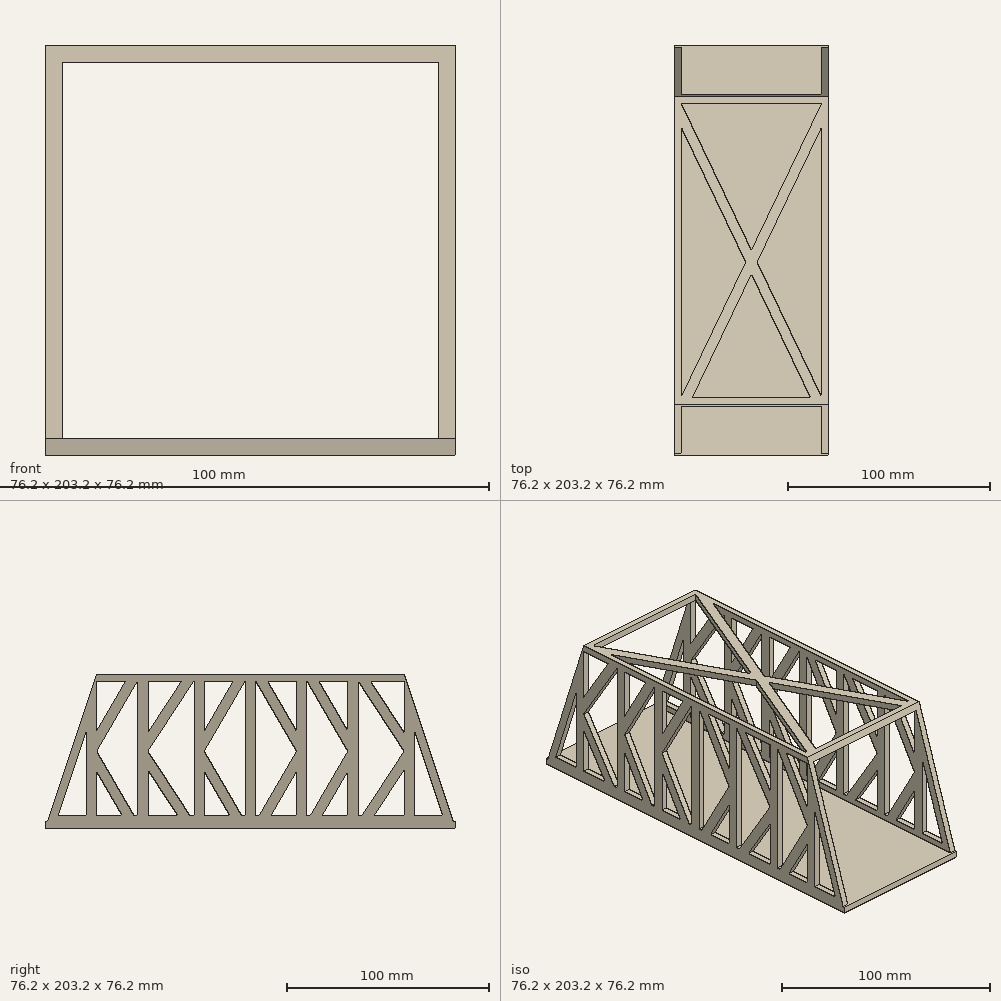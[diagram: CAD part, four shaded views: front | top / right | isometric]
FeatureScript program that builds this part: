
annotation { "Feature Type Name" : "Feature", "Feature Type Description" : "" }
export const myFeature = defineFeature(function(context is Context, id is Id, definition is map)
    precondition{}
    {
        {
            var Q0;
            Q0=qCreatedBy(makeId("Right.planeOp"),FACE);
            var sketch = newSketch(context, id + "F0", { "sketchPlane" : qUnion([Q0])});
            skLineSegment(sketch, "E0", {"start": v(-101.6, -38.1) * mm, "end": v(101.6, -38.1) * mm});
            skLineSegment(sketch, "E1", {"start": v(-76.2, 38.1) * mm, "end": v(76.2, 38.1) * mm});
            skLineSegment(sketch, "E2", {"start": v(-76.2, 38.1) * mm, "end": v(-101.6, -38.1) * mm});
            skLineSegment(sketch, "E3", {"start": v(76.2, 38.1) * mm, "end": v(101.6, -38.1) * mm});
            skSolve(sketch);
        }
        {
            var Q0;
            Q0=qSketchRegion(id+"F0",true);
            extrude(context, id + "F1", {"entities" : qUnion([Q0]), "endBound" : BoundingType.SYMMETRIC, "depth" : 76.2 * mm, "offsetDistance" : 25.4 * mm});
        }
        {
            var Q0;
            Q0=qCreatedBy(makeId("Front.planeOp"),FACE);
            var sketch = newSketch(context, id + "F2", { "sketchPlane" : qUnion([Q0])});
            skLineSegment(sketch, "E4.bottom", {"start": v(34.92, -34.92) * mm, "end": v(-34.92, -34.93) * mm});
            skLineSegment(sketch, "E4.top", {"start": v(34.92, 34.93) * mm, "end": v(-34.92, 34.92) * mm});
            skLineSegment(sketch, "E4.left", {"start": v(-34.92, -34.92) * mm, "end": v(-34.92, 34.92) * mm});
            skLineSegment(sketch, "E4.right", {"start": v(34.92, -34.92) * mm, "end": v(34.92, 34.92) * mm});
            skPoint(sketch, "E4.middle", {"position": v(0, 0) * mm});
            skSolve(sketch);
        }
        {
            var Q0;
            Q0=qSketchRegion(id+"F2",true);
            extrude(context, id + "F3", {"entities" : qUnion([Q0]), "operationType" : NewBodyOperationType.REMOVE, "endBound" : BoundingType.SYMMETRIC, "oppositeDirection" : true, "depth" : 254 * mm, "offsetDistance" : 25.4 * mm});
        }
        {
            var Q0;
            Q0=makeQuery(id+"F1.opExtrude","CAP_FACE",FACE,{"disambiguationData":[OSD([sQuery(id+"F0.wireOp",EDGE,"E0"),sQuery(id+"F0.wireOp",EDGE,"E1"),sQuery(id+"F0.wireOp",EDGE,"E2"),sQuery(id+"F0.wireOp",EDGE,"E3")])],"isStart":false});
            var sketch = newSketch(context, id + "F4", { "sketchPlane" : qUnion([Q0])});
            skLineSegment(sketch, "E5.bottom", {"start": v(76.2, -34.92) * mm, "end": v(-76.2, -34.92) * mm});
            skLineSegment(sketch, "E5.top", {"start": v(76.2, 34.92) * mm, "end": v(-76.2, 34.92) * mm});
            skLineSegment(sketch, "E5.left", {"start": v(76.2, -34.92) * mm, "end": v(76.2, 34.92) * mm});
            skLineSegment(sketch, "E5.right", {"start": v(-76.2, -34.92) * mm, "end": v(-76.2, 34.92) * mm});
            skPoint(sketch, "E5.middle", {"position": v(0, 0) * mm});
            skLineSegment(sketch, "E6.bottom", {"start": v(2.54, -34.92) * mm, "end": v(-2.54, -34.92) * mm});
            skLineSegment(sketch, "E6.top", {"start": v(2.54, 34.92) * mm, "end": v(-2.54, 34.92) * mm});
            skLineSegment(sketch, "E6.left", {"start": v(2.54, -34.93) * mm, "end": v(2.54, 34.93) * mm});
            skLineSegment(sketch, "E6.right", {"start": v(-2.54, -34.93) * mm, "end": v(-2.54, 34.93) * mm});
            skLineSegment(sketch, "E7.bottom", {"start": v(-50.8, -34.92) * mm, "end": v(-55.88, -34.92) * mm});
            skLineSegment(sketch, "E7.top", {"start": v(-50.8, 34.92) * mm, "end": v(-55.88, 34.92) * mm});
            skLineSegment(sketch, "E7.left", {"start": v(-50.8, -34.93) * mm, "end": v(-50.8, 34.93) * mm});
            skLineSegment(sketch, "E7.right", {"start": v(-55.88, -34.93) * mm, "end": v(-55.88, 34.93) * mm});
            skPoint(sketch, "E7.middle", {"position": v(-53.34, 0) * mm});
            skLineSegment(sketch, "E8.bottom", {"start": v(-22.86, -34.92) * mm, "end": v(-27.94, -34.92) * mm});
            skLineSegment(sketch, "E8.top", {"start": v(-22.86, 34.92) * mm, "end": v(-27.94, 34.92) * mm});
            skLineSegment(sketch, "E8.left", {"start": v(-22.86, -34.92) * mm, "end": v(-22.86, 34.92) * mm});
            skLineSegment(sketch, "E8.right", {"start": v(-27.94, -34.92) * mm, "end": v(-27.94, 34.92) * mm});
            skPoint(sketch, "E8.middle", {"position": v(-25.4, 0) * mm});
            skLineSegment(sketch, "E9.bottom", {"start": v(27.94, -34.92) * mm, "end": v(22.86, -34.92) * mm});
            skLineSegment(sketch, "E9.top", {"start": v(27.94, 34.92) * mm, "end": v(22.86, 34.92) * mm});
            skLineSegment(sketch, "E9.left", {"start": v(27.94, -34.92) * mm, "end": v(27.94, 34.92) * mm});
            skLineSegment(sketch, "E9.right", {"start": v(22.86, -34.93) * mm, "end": v(22.86, 34.92) * mm});
            skPoint(sketch, "E9.middle", {"position": v(25.4, 0) * mm});
            skLineSegment(sketch, "E10.bottom", {"start": v(53.34, -34.92) * mm, "end": v(48.26, -34.92) * mm});
            skLineSegment(sketch, "E10.top", {"start": v(53.34, 34.92) * mm, "end": v(48.26, 34.92) * mm});
            skLineSegment(sketch, "E10.left", {"start": v(53.34, -34.93) * mm, "end": v(53.34, 34.93) * mm});
            skLineSegment(sketch, "E10.right", {"start": v(48.26, -34.93) * mm, "end": v(48.26, 34.93) * mm});
            skPoint(sketch, "E10.middle", {"position": v(50.8, 0) * mm});
            skLineSegment(sketch, "E11", {"start": v(-55.88, 34.92) * mm, "end": v(-76.2, 0) * mm});
            skLineSegment(sketch, "E12", {"start": v(-76.2, 0) * mm, "end": v(-55.88, -34.92) * mm});
            skLineSegment(sketch, "E13", {"start": v(-27.94, 34.92) * mm, "end": v(-50.8, 0) * mm});
            skLineSegment(sketch, "E14", {"start": v(-50.8, 0) * mm, "end": v(-27.94, -34.92) * mm});
            skLineSegment(sketch, "E15", {"start": v(-2.54, 34.92) * mm, "end": v(-22.86, 0) * mm});
            skLineSegment(sketch, "E16", {"start": v(-22.86, 0) * mm, "end": v(-2.54, -34.92) * mm});
            skLineSegment(sketch, "E17", {"start": v(2.54, 34.92) * mm, "end": v(22.86, 0) * mm});
            skLineSegment(sketch, "E18", {"start": v(22.86, 0) * mm, "end": v(2.54, -34.92) * mm});
            skLineSegment(sketch, "E19", {"start": v(27.94, 34.93) * mm, "end": v(48.26, 0) * mm});
            skLineSegment(sketch, "E20", {"start": v(48.26, 0) * mm, "end": v(27.94, -34.93) * mm});
            skLineSegment(sketch, "E21", {"start": v(53.34, 34.92) * mm, "end": v(76.2, 0) * mm});
            skLineSegment(sketch, "E22", {"start": v(76.2, 0) * mm, "end": v(53.34, -34.92) * mm});
            skLineSegment(sketch, "E23", {"start": v(-76.2, -10.1) * mm, "end": v(-61.76, -34.93) * mm});
            skLineSegment(sketch, "E24", {"start": v(-34.01, 34.93) * mm, "end": v(-50.8, 9.28) * mm});
            skLineSegment(sketch, "E25", {"start": v(-50.8, -9.28) * mm, "end": v(-34.01, -34.93) * mm});
            skLineSegment(sketch, "E26", {"start": v(-8.42, 34.93) * mm, "end": v(-22.86, 10.1) * mm});
            skLineSegment(sketch, "E27", {"start": v(-22.86, -10.1) * mm, "end": v(-8.42, -34.93) * mm});
            skLineSegment(sketch, "E28", {"start": v(-61.76, 34.93) * mm, "end": v(-76.2, 10.1) * mm});
            skLineSegment(sketch, "E29", {"start": v(8.42, 34.93) * mm, "end": v(22.86, 10.1) * mm});
            skLineSegment(sketch, "E30", {"start": v(22.86, -10.1) * mm, "end": v(8.42, -34.93) * mm});
            skLineSegment(sketch, "E31", {"start": v(33.82, 34.93) * mm, "end": v(48.26, 10.1) * mm});
            skLineSegment(sketch, "E32", {"start": v(48.26, -10.1) * mm, "end": v(33.82, -34.93) * mm});
            skLineSegment(sketch, "E33", {"start": v(59.41, 34.93) * mm, "end": v(76.2, 9.28) * mm});
            skLineSegment(sketch, "E34", {"start": v(76.2, -9.28) * mm, "end": v(59.41, -34.93) * mm});
            skLineSegment(sketch, "E35", {"start": v(-81.28, -34.93) * mm, "end": v(-81.28, 10.1) * mm});
            skLineSegment(sketch, "E36", {"start": v(-81.28, 10.1) * mm, "end": v(-96.29, -34.93) * mm});
            skLineSegment(sketch, "E37", {"start": v(-96.29, -34.92) * mm, "end": v(-81.28, -34.92) * mm});
            skLineSegment(sketch, "E38.MirrorCS", {"start": v(81.28, -34.93) * mm, "end": v(81.28, 10.1) * mm});
            skLineSegment(sketch, "E39.MirrorCS", {"start": v(81.28, 10.1) * mm, "end": v(96.29, -34.93) * mm});
            skLineSegment(sketch, "E40.MirrorCS", {"start": v(96.29, -34.92) * mm, "end": v(81.28, -34.92) * mm});
            skSolve(sketch);
        }
        {
            var Q0;
            Q0=makeQuery(id+"F4.imprint","IMPRINT",FACE,{"disambiguationData":[TD([[makeQuery(id+"F4.imprint","IMPRINT",EDGE,{"derivedFrom":sQuery(id+"F4.wireOp",EDGE,"E35")}),1.0]])]});
            var Q1;
            {var subQ3=sQuery(id+"F4.wireOp",EDGE,"E28");Q1=makeQuery(id+"F4.imprint","IMPRINT",FACE,{"disambiguationData":[TD([[makeQuery(id+"F4.imprint","IMPRINT",EDGE,{"derivedFrom":subQ3}),-1.0]])]});}
            var Q2;
            Q2=makeQuery(id+"F4.imprint","IMPRINT",FACE,{"disambiguationData":[TD([[makeQuery(id+"F4.imprint","IMPRINT",EDGE,{"derivedFrom":sQuery(id+"F4.wireOp",EDGE,"E7.right")}),1.0]])]});
            var Q3;
            {var subQ3=sQuery(id+"F4.wireOp",EDGE,"E23");Q3=makeQuery(id+"F4.imprint","IMPRINT",FACE,{"disambiguationData":[TD([[makeQuery(id+"F4.imprint","IMPRINT",EDGE,{"derivedFrom":subQ3}),-1.0]])]});}
            var Q4;
            {var subQ3=sQuery(id+"F4.wireOp",EDGE,"E24");Q4=makeQuery(id+"F4.imprint","IMPRINT",FACE,{"disambiguationData":[TD([[makeQuery(id+"F4.imprint","IMPRINT",EDGE,{"derivedFrom":subQ3}),-1.0]])]});}
            var Q5;
            Q5=makeQuery(id+"F4.imprint","IMPRINT",FACE,{"disambiguationData":[TD([[makeQuery(id+"F4.imprint","IMPRINT",EDGE,{"derivedFrom":sQuery(id+"F4.wireOp",EDGE,"E8.right")}),1.0]])]});
            var Q6;
            {var subQ3=sQuery(id+"F4.wireOp",EDGE,"E25");Q6=makeQuery(id+"F4.imprint","IMPRINT",FACE,{"disambiguationData":[TD([[makeQuery(id+"F4.imprint","IMPRINT",EDGE,{"derivedFrom":subQ3}),-1.0]])]});}
            var Q7;
            {var subQ3=sQuery(id+"F4.wireOp",EDGE,"E26");Q7=makeQuery(id+"F4.imprint","IMPRINT",FACE,{"disambiguationData":[TD([[makeQuery(id+"F4.imprint","IMPRINT",EDGE,{"derivedFrom":subQ3}),-1.0]])]});}
            var Q8;
            Q8=makeQuery(id+"F4.imprint","IMPRINT",FACE,{"disambiguationData":[TD([[makeQuery(id+"F4.imprint","IMPRINT",EDGE,{"derivedFrom":sQuery(id+"F4.wireOp",EDGE,"E6.right")}),1.0]])]});
            var Q9;
            {var subQ3=sQuery(id+"F4.wireOp",EDGE,"E27");Q9=makeQuery(id+"F4.imprint","IMPRINT",FACE,{"disambiguationData":[TD([[makeQuery(id+"F4.imprint","IMPRINT",EDGE,{"derivedFrom":subQ3}),-1.0]])]});}
            var Q10;
            Q10=makeQuery(id+"F4.imprint","IMPRINT",FACE,{"disambiguationData":[TD([[makeQuery(id+"F4.imprint","IMPRINT",EDGE,{"derivedFrom":sQuery(id+"F4.wireOp",EDGE,"E6.left")}),-1.0]])]});
            var Q11;
            {var subQ3=sQuery(id+"F4.wireOp",EDGE,"E29");Q11=makeQuery(id+"F4.imprint","IMPRINT",FACE,{"disambiguationData":[TD([[makeQuery(id+"F4.imprint","IMPRINT",EDGE,{"derivedFrom":subQ3}),1.0]])]});}
            var Q12;
            Q12=makeQuery(id+"F4.imprint","IMPRINT",FACE,{"disambiguationData":[TD([[makeQuery(id+"F4.imprint","IMPRINT",EDGE,{"derivedFrom":sQuery(id+"F4.wireOp",EDGE,"E9.left")}),-1.0]])]});
            var Q13;
            {var subQ3=sQuery(id+"F4.wireOp",EDGE,"E30");Q13=makeQuery(id+"F4.imprint","IMPRINT",FACE,{"disambiguationData":[TD([[makeQuery(id+"F4.imprint","IMPRINT",EDGE,{"derivedFrom":subQ3}),1.0]])]});}
            var Q14;
            {var subQ3=sQuery(id+"F4.wireOp",EDGE,"E31");Q14=makeQuery(id+"F4.imprint","IMPRINT",FACE,{"disambiguationData":[TD([[makeQuery(id+"F4.imprint","IMPRINT",EDGE,{"derivedFrom":subQ3}),1.0]])]});}
            var Q15;
            {var subQ3=sQuery(id+"F4.wireOp",EDGE,"E32");Q15=makeQuery(id+"F4.imprint","IMPRINT",FACE,{"disambiguationData":[TD([[makeQuery(id+"F4.imprint","IMPRINT",EDGE,{"derivedFrom":subQ3}),1.0]])]});}
            var Q16;
            Q16=makeQuery(id+"F4.imprint","IMPRINT",FACE,{"disambiguationData":[TD([[makeQuery(id+"F4.imprint","IMPRINT",EDGE,{"derivedFrom":sQuery(id+"F4.wireOp",EDGE,"E10.left")}),-1.0]])]});
            var Q17;
            {var subQ3=sQuery(id+"F4.wireOp",EDGE,"E33");Q17=makeQuery(id+"F4.imprint","IMPRINT",FACE,{"disambiguationData":[TD([[makeQuery(id+"F4.imprint","IMPRINT",EDGE,{"derivedFrom":subQ3}),1.0]])]});}
            var Q18;
            {var subQ3=sQuery(id+"F4.wireOp",EDGE,"E34");Q18=makeQuery(id+"F4.imprint","IMPRINT",FACE,{"disambiguationData":[TD([[makeQuery(id+"F4.imprint","IMPRINT",EDGE,{"derivedFrom":subQ3}),1.0]])]});}
            var Q19;
            Q19=makeQuery(id+"F4.imprint","IMPRINT",FACE,{"disambiguationData":[TD([[makeQuery(id+"F4.imprint","IMPRINT",EDGE,{"derivedFrom":sQuery(id+"F4.wireOp",EDGE,"E38.MirrorCS")}),-1.0]])]});
            extrude(context, id + "F5", {"entities" : qUnion([Q0, Q1, Q2, Q3, Q4, Q5, Q6, Q7, Q8, Q9, Q10, Q11, Q12, Q13, Q14, Q15, Q16, Q17, Q18, Q19]), "operationType" : NewBodyOperationType.REMOVE, "oppositeDirection" : true, "depth" : 76.2 * mm, "offsetDistance" : 25.4 * mm});
        }
        {
            var Q0;
            Q0=makeQuery(id+"F1.opExtrude","CAP_FACE",FACE,{"disambiguationData":[OSD([sQuery(id+"F0.wireOp",EDGE,"E0"),sQuery(id+"F0.wireOp",EDGE,"E1"),sQuery(id+"F0.wireOp",EDGE,"E2"),sQuery(id+"F0.wireOp",EDGE,"E3")])],"isStart":false});
            var sketch = newSketch(context, id + "F6", { "sketchPlane" : qUnion([Q0])});
            skLineSegment(sketch, "E41.bottom", {"start": v(-96.29, -34.93) * mm, "end": v(-101.6, -34.93) * mm});
            skLineSegment(sketch, "E41.top", {"start": v(-96.29, -38.1) * mm, "end": v(-101.6, -38.1) * mm});
            skLineSegment(sketch, "E41.left", {"start": v(-96.29, -34.93) * mm, "end": v(-96.29, -38.1) * mm});
            skLineSegment(sketch, "E41.right", {"start": v(-101.6, -34.93) * mm, "end": v(-101.6, -38.1) * mm});
            skLineSegment(sketch, "E42.MirrorCS", {"start": v(96.29, -34.93) * mm, "end": v(101.6, -34.93) * mm});
            skLineSegment(sketch, "E43.MirrorCS", {"start": v(101.6, -34.93) * mm, "end": v(101.6, -38.1) * mm});
            skLineSegment(sketch, "E44.MirrorCS", {"start": v(96.29, -34.93) * mm, "end": v(96.29, -38.1) * mm});
            skLineSegment(sketch, "E45.MirrorCS", {"start": v(96.29, -38.1) * mm, "end": v(101.6, -38.1) * mm});
            skSolve(sketch);
        }
        {
            var Q0;
            Q0=qSketchRegion(id+"F6",true);
            extrude(context, id + "F7", {"entities" : qUnion([Q0]), "operationType" : NewBodyOperationType.ADD, "oppositeDirection" : true, "depth" : 76.2 * mm, "offsetDistance" : 25.4 * mm});
        }
        {
            var Q0;
            Q0=makeQuery(id+"F1.opExtrude","SWEPT_FACE",FACE,{"disambiguationData":[OSD([sQuery(id+"F0.wireOp",EDGE,"E1")])]});
            var sketch = newSketch(context, id + "F8", { "sketchPlane" : qUnion([Q0])});
            skLineSegment(sketch, "E46.bottom", {"start": v(34.92, -73.03) * mm, "end": v(-34.93, -73.03) * mm});
            skLineSegment(sketch, "E46.top", {"start": v(34.92, 73.03) * mm, "end": v(-34.93, 73.03) * mm});
            skLineSegment(sketch, "E46.left", {"start": v(34.92, -73.03) * mm, "end": v(34.92, 73.03) * mm});
            skLineSegment(sketch, "E46.right", {"start": v(-34.92, -73.03) * mm, "end": v(-34.92, 73.03) * mm});
            skPoint(sketch, "E46.middle", {"position": v(0, 0) * mm});
            skLineSegment(sketch, "E47", {"start": v(-34.92, 73.03) * mm, "end": v(34.92, -73.03) * mm});
            skLineSegment(sketch, "E48", {"start": v(-34.92, -73.03) * mm, "end": v(34.92, 73.03) * mm});
            skLineSegment(sketch, "E49", {"start": v(-34.92, 61.25) * mm, "end": v(29.3, -73.03) * mm});
            skLineSegment(sketch, "E50", {"start": v(34.92, 61.25) * mm, "end": v(-29.3, -73.03) * mm});
            skSolve(sketch);
        }
        {
            var Q0;
            {var subQ1=sQuery(id+"F8.wireOp",EDGE,"E46.right");var subQ3=sQuery(id+"F8.wireOp",EDGE,"E49");var subQ4=makeQuery(id+"F8.imprint","INTERSECT",VERTEX,{"derivedFrom":[subQ1,subQ3]});Q0=makeQuery(id+"F8.imprint","IMPRINT",FACE,{"disambiguationData":[TD([[makeQuery(id+"F8.imprint","IMPRINT",EDGE,{"disambiguationData":[TD([[subQ4,-1.0]])],"derivedFrom":subQ3}),-1.0]])]});}
            var Q1;
            {var subQ0=sQuery(id+"F8.wireOp",EDGE,"E46.top");Q1=makeQuery(id+"F8.imprint","IMPRINT",FACE,{"disambiguationData":[TD([[makeQuery(id+"F8.imprint","IMPRINT",EDGE,{"derivedFrom":subQ0}),1.0]])]});}
            var Q2;
            {var subQ1=sQuery(id+"F8.wireOp",EDGE,"E46.left");var subQ3=sQuery(id+"F8.wireOp",EDGE,"E50");var subQ4=makeQuery(id+"F8.imprint","INTERSECT",VERTEX,{"derivedFrom":[subQ1,subQ3]});Q2=makeQuery(id+"F8.imprint","IMPRINT",FACE,{"disambiguationData":[TD([[makeQuery(id+"F8.imprint","IMPRINT",EDGE,{"disambiguationData":[TD([[subQ4,-1.0]])],"derivedFrom":subQ3}),1.0]])]});}
            var Q3;
            {var subQ0=sQuery(id+"F8.wireOp",EDGE,"E49");var subQ1=sQuery(id+"F8.wireOp",EDGE,"E46.bottom");var subQ2=makeQuery(id+"F8.imprint","INTERSECT",VERTEX,{"derivedFrom":[subQ1,subQ0]});Q3=makeQuery(id+"F8.imprint","IMPRINT",FACE,{"disambiguationData":[TD([[makeQuery(id+"F8.imprint","IMPRINT",EDGE,{"disambiguationData":[TD([[subQ2,-1.0]])],"derivedFrom":subQ1}),-1.0]])]});}
            extrude(context, id + "F9", {"entities" : qUnion([Q0, Q1, Q2, Q3]), "operationType" : NewBodyOperationType.REMOVE, "oppositeDirection" : true, "depth" : 3.17 * mm, "offsetDistance" : 25.4 * mm});
        }
        {
            var Q0;
            {var subQ0=sQuery(id+"F4.wireOp",EDGE,"E5.bottom");Q0=makeQuery(id+"F7.boolean.opBoolean","MERGE",FACE,{"derivedFrom":[makeQuery(id+"F5.boolean.opBoolean","MERGE",FACE,{"derivedFrom":[makeQuery(id+"F3.boolean.opBoolean","COPY",FACE,{"derivedFrom":makeQuery(id+"F3.opExtrude","SWEPT_FACE",FACE,{"disambiguationData":[OSD([sQuery(id+"F2.wireOp",EDGE,"E4.bottom")])]})})],"fromTools":[makeQuery(id+"F5.opExtrude","SWEPT_FACE",FACE,{"disambiguationData":[OSD([subQ0]),TDD([makeQuery(id+"F4.imprint","IMPRINT",EDGE,{"disambiguationData":[TD([[makeQuery(id+"F4.imprint","INTERSECT",VERTEX,{"derivedFrom":[subQ0,sQuery(id+"F4.wireOp",EDGE,"E5.left")]}),-1.0]])],"derivedFrom":subQ0})])]}),makeQuery(id+"F5.opExtrude","SWEPT_FACE",FACE,{"disambiguationData":[OSD([subQ0]),TDD([makeQuery(id+"F4.imprint","IMPRINT",EDGE,{"disambiguationData":[TD([[makeQuery(id+"F4.imprint","INTERSECT",VERTEX,{"derivedFrom":[subQ0,sQuery(id+"F4.wireOp",EDGE,"E32")]}),1.0]])],"derivedFrom":subQ0})])]}),makeQuery(id+"F5.opExtrude","SWEPT_FACE",FACE,{"disambiguationData":[OSD([subQ0]),TDD([makeQuery(id+"F4.imprint","IMPRINT",EDGE,{"disambiguationData":[TD([[makeQuery(id+"F4.imprint","INTERSECT",VERTEX,{"derivedFrom":[subQ0,sQuery(id+"F4.wireOp",EDGE,"E30")]}),1.0]])],"derivedFrom":subQ0})])]}),makeQuery(id+"F5.opExtrude","SWEPT_FACE",FACE,{"disambiguationData":[OSD([subQ0]),TDD([makeQuery(id+"F4.imprint","IMPRINT",EDGE,{"disambiguationData":[TD([[makeQuery(id+"F4.imprint","INTERSECT",VERTEX,{"derivedFrom":[subQ0,sQuery(id+"F4.wireOp",EDGE,"E27")]}),-1.0]])],"derivedFrom":subQ0})])]}),makeQuery(id+"F5.opExtrude","SWEPT_FACE",FACE,{"disambiguationData":[OSD([subQ0]),TDD([makeQuery(id+"F4.imprint","IMPRINT",EDGE,{"disambiguationData":[TD([[makeQuery(id+"F4.imprint","INTERSECT",VERTEX,{"derivedFrom":[subQ0,sQuery(id+"F4.wireOp",EDGE,"E25")]}),-1.0]])],"derivedFrom":subQ0})])]}),makeQuery(id+"F5.opExtrude","SWEPT_FACE",FACE,{"disambiguationData":[OSD([subQ0]),TDD([makeQuery(id+"F4.imprint","IMPRINT",EDGE,{"disambiguationData":[TD([[makeQuery(id+"F4.imprint","INTERSECT",VERTEX,{"derivedFrom":[subQ0,sQuery(id+"F4.wireOp",EDGE,"E5.right")]}),1.0]])],"derivedFrom":subQ0})])]}),makeQuery(id+"F5.opExtrude","SWEPT_FACE",FACE,{"disambiguationData":[OSD([sQuery(id+"F4.wireOp",EDGE,"E37")])]}),makeQuery(id+"F5.opExtrude","SWEPT_FACE",FACE,{"disambiguationData":[OSD([sQuery(id+"F4.wireOp",EDGE,"E40.MirrorCS")])]})]}),makeQuery(id+"F7.opExtrude","SWEPT_FACE",FACE,{"disambiguationData":[OSD([sQuery(id+"F6.wireOp",EDGE,"E41.bottom")])]}),makeQuery(id+"F7.opExtrude","SWEPT_FACE",FACE,{"disambiguationData":[OSD([sQuery(id+"F6.wireOp",EDGE,"E42.MirrorCS")])]})]});}
            var sketch = newSketch(context, id + "F10", { "sketchPlane" : qUnion([Q0])});
            skLineSegment(sketch, "E51.bottom", {"start": v(34.92, 96.29) * mm, "end": v(38.1, 96.29) * mm});
            skLineSegment(sketch, "E51.top", {"start": v(34.92, -96.29) * mm, "end": v(38.1, -96.29) * mm});
            skLineSegment(sketch, "E51.left", {"start": v(34.92, 96.29) * mm, "end": v(34.92, -96.29) * mm});
            skLineSegment(sketch, "E51.right", {"start": v(38.1, 96.29) * mm, "end": v(38.1, -96.29) * mm});
            skLineSegment(sketch, "E52.MirrorCS", {"start": v(-38.1, 96.29) * mm, "end": v(-38.1, -96.29) * mm});
            skLineSegment(sketch, "E53.MirrorCS", {"start": v(-34.92, 96.29) * mm, "end": v(-34.92, -96.29) * mm});
            skLineSegment(sketch, "E54", {"start": v(-38.1, -96.29) * mm, "end": v(-34.92, -96.29) * mm});
            skLineSegment(sketch, "E55", {"start": v(-38.1, 96.29) * mm, "end": v(-34.92, 96.29) * mm});
            skSolve(sketch);
        }
        {
            var Q0;
            Q0=qSketchRegion(id+"F10",true);
            extrude(context, id + "F11", {"entities" : qUnion([Q0]), "operationType" : NewBodyOperationType.ADD, "depth" : 3.17 * mm, "offsetDistance" : 25.4 * mm});
        }
    });
